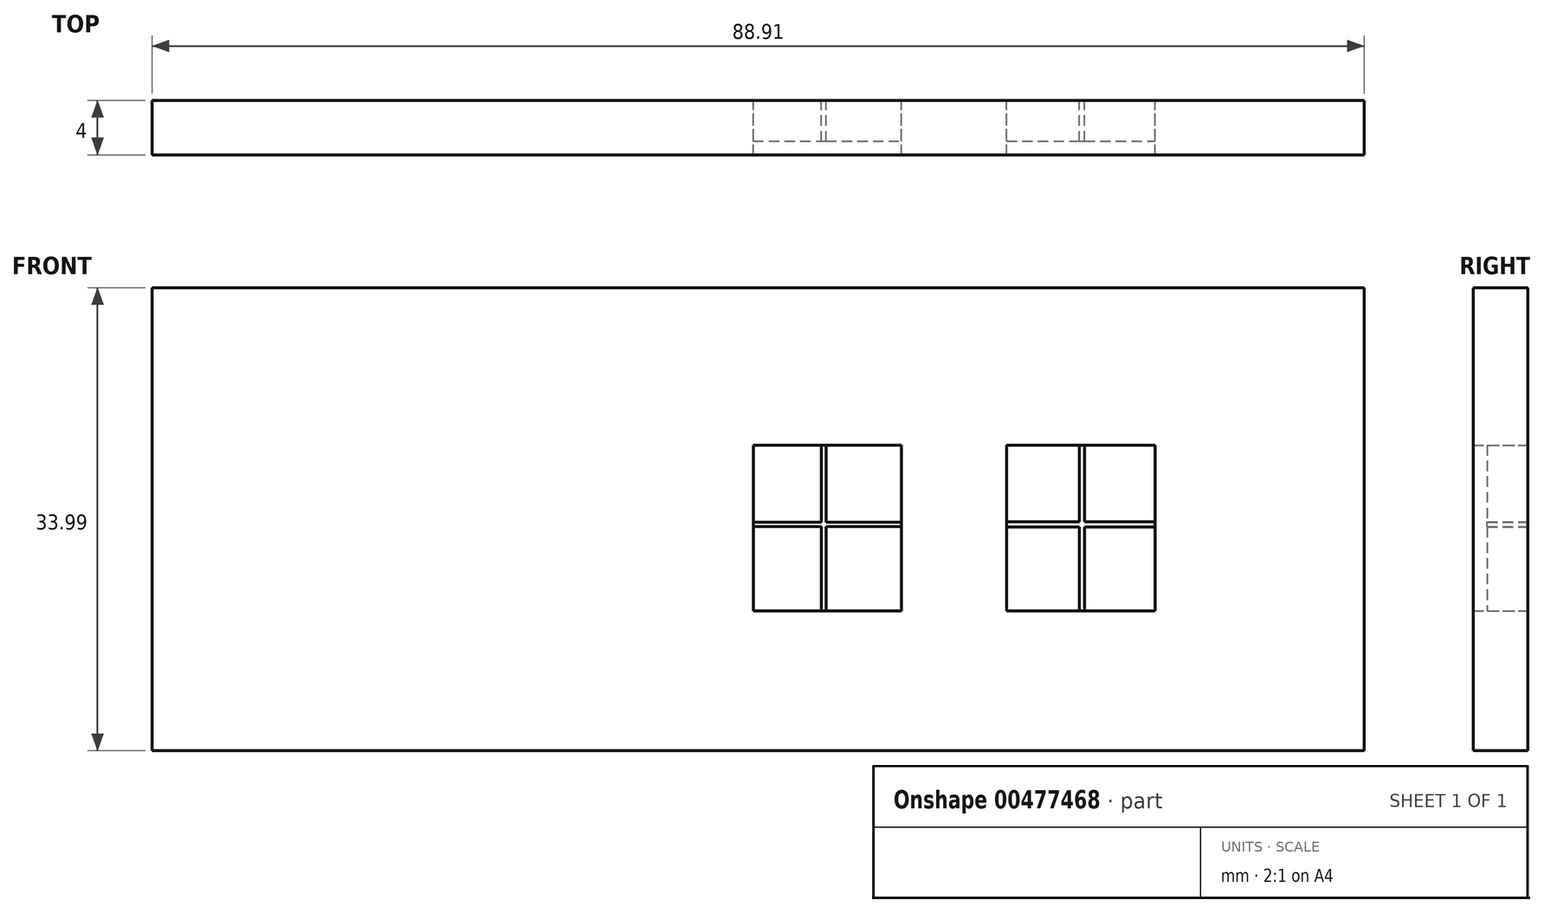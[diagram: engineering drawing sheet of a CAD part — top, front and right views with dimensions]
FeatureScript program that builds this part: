
annotation { "Feature Type Name" : "Feature", "Feature Type Description" : "" }
export const myFeature = defineFeature(function(context is Context, id is Id, definition is map)
    precondition{}
    {
        {
            var Q0;
            Q0=qCreatedBy(makeId("Front.planeOp"),FACE);
            var sketch = newSketch(context, id + "F0", { "sketchPlane" : qUnion([Q0])});
            skLineSegment(sketch, "E0.bottom", {"start": v(-35.52, 16.4) * mm, "end": v(53.39, 16.4) * mm});
            skLineSegment(sketch, "E0.top", {"start": v(-35.52, -17.6) * mm, "end": v(53.39, -17.6) * mm});
            skLineSegment(sketch, "E0.left", {"start": v(-35.52, 16.4) * mm, "end": v(-35.52, -17.6) * mm});
            skLineSegment(sketch, "E0.right", {"start": v(53.39, 16.4) * mm, "end": v(53.39, -17.6) * mm});
            skLineSegment(sketch, "E1.bottom", {"start": v(27.15, -7.34) * mm, "end": v(38.03, -7.34) * mm});
            skLineSegment(sketch, "E1.top", {"start": v(27.15, 4.82) * mm, "end": v(38.03, 4.82) * mm});
            skLineSegment(sketch, "E1.left", {"start": v(27.15, -7.34) * mm, "end": v(27.15, 4.82) * mm});
            skLineSegment(sketch, "E1.right", {"start": v(38.03, -7.34) * mm, "end": v(38.03, 4.82) * mm});
            skLineSegment(sketch, "E2.bottom", {"start": v(8.57, -7.34) * mm, "end": v(19.44, -7.34) * mm});
            skLineSegment(sketch, "E2.top", {"start": v(8.57, 4.83) * mm, "end": v(19.44, 4.83) * mm});
            skLineSegment(sketch, "E2.left", {"start": v(8.57, -7.34) * mm, "end": v(8.57, 4.83) * mm});
            skLineSegment(sketch, "E2.right", {"start": v(19.44, -7.34) * mm, "end": v(19.44, 4.83) * mm});
            skLineSegment(sketch, "E3.bottom", {"start": v(13.36, 4.83) * mm, "end": v(13.66, 4.83) * mm});
            skLineSegment(sketch, "E3.top", {"start": v(13.36, -7.34) * mm, "end": v(13.66, -7.34) * mm});
            skSolve(sketch);
        }
        {
            var Q0;
            Q0 = qSketchRegion(id + "F0", true);
            extrude(context, id + "F1", {"entities" : qUnion([Q0]), "depth" : 4 * mm});
        }
        {
            var Q0;
            Q0=qCreatedBy(makeId("Front.planeOp"),FACE);
            var sketch = newSketch(context, id + "F2", { "sketchPlane" : qUnion([Q0])});
            skLineSegment(sketch, "E4.bottom", {"start": v(8.39, -0.82) * mm, "end": v(19.67, -0.82) * mm});
            skLineSegment(sketch, "E4.top", {"start": v(8.39, -1.16) * mm, "end": v(19.67, -1.16) * mm});
            skLineSegment(sketch, "E4.left", {"start": v(8.39, -0.82) * mm, "end": v(8.39, -1.16) * mm});
            skLineSegment(sketch, "E4.right", {"start": v(19.67, -0.82) * mm, "end": v(19.67, -1.16) * mm});
            skLineSegment(sketch, "E5.bottom", {"start": v(13.57, 5) * mm, "end": v(13.91, 5) * mm});
            skLineSegment(sketch, "E5.top", {"start": v(13.57, -7.88) * mm, "end": v(13.91, -7.88) * mm});
            skLineSegment(sketch, "E5.left", {"start": v(13.57, 5) * mm, "end": v(13.57, -7.88) * mm});
            skLineSegment(sketch, "E5.right", {"start": v(13.91, 5) * mm, "end": v(13.91, -7.88) * mm});
            skLineSegment(sketch, "E6.bottom", {"start": v(32.49, 5.22) * mm, "end": v(32.87, 5.22) * mm});
            skLineSegment(sketch, "E6.top", {"start": v(32.49, -7.7) * mm, "end": v(32.87, -7.7) * mm});
            skLineSegment(sketch, "E6.left", {"start": v(32.49, 5.22) * mm, "end": v(32.49, -7.7) * mm});
            skLineSegment(sketch, "E6.right", {"start": v(32.87, 5.22) * mm, "end": v(32.87, -7.7) * mm});
            skLineSegment(sketch, "E7.bottom", {"start": v(26.89, -0.8) * mm, "end": v(38.22, -0.8) * mm});
            skLineSegment(sketch, "E7.top", {"start": v(26.89, -1.18) * mm, "end": v(38.22, -1.18) * mm});
            skLineSegment(sketch, "E7.left", {"start": v(26.89, -0.8) * mm, "end": v(26.89, -1.18) * mm});
            skLineSegment(sketch, "E7.right", {"start": v(38.22, -0.8) * mm, "end": v(38.22, -1.18) * mm});
            skSolve(sketch);
        }
        {
            var Q0;
            Q0 = qSketchRegion(id + "F2", true);
            extrude(context, id + "F3", {"entities" : qUnion([Q0]), "operationType" : NewBodyOperationType.ADD, "depth" : 3 * mm});
        }
    });
